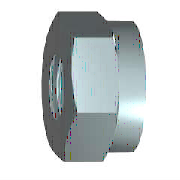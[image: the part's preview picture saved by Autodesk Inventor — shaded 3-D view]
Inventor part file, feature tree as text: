
AUTODESK INVENTOR PART (.ipt)
format: ipt  version: 2015 (Build 190159000, 159)  size: 194,048 bytes
history: native  units: mm (DEFAULTED — no unit token found)
features: sketch x4, extrude x1, chamfer x1, hole x1, other x1, plane x1, fillet x1
ambient origin geometry x7: Origin, YZ Plane, XZ Plane, X Axis, Y Axis, Z Axis, Center Point
bodies: Solid1 (feature_tree), Body (feature_tree)
feature tree (10):
  extrude  "Ring"  Depth=6.44mm
  chamfer  "Chamfer1"  Distance=11.63mm
  hole  "Thread"  [1 undecoded]
  other  "Work Axis1"
  plane  "Work Plane1"
  fillet  "Fillet1"  [1 undecoded]
  sketch  "Sketch1"  dims[d0=15.011107mm d1=6.44mm]
  sketch  "Sketch3"  dims[d3=30.0deg]
  sketch  "Sketch2"  dims[d2=0.0mm]
  sketch  "Sketch4"  dims[d4=30.0deg d5=11.63mm d6=11.63mm d26=90.0deg d7=11.63mm d8=3.06mm d9=0.0mm d30=6.647mm d31=6.0mm d32=4.0mm d33=2.0mm d34=14.3117mm d35=8.0mm d36=20.594885mm d10=0.676582mm d11=30.0deg d12=0.676582mm d13=30.0deg d14=0.0mm d15=0.0mm d45=0.0mm d46=0.676582mm d47=0.676582mm d48=0.0mm d49=1.25mm]
note: 2 required parameter values undecoded (feature->parameter linkage not recoverable at this tier; creation-order binding heuristic only, values carry confidence <= 0.55)
